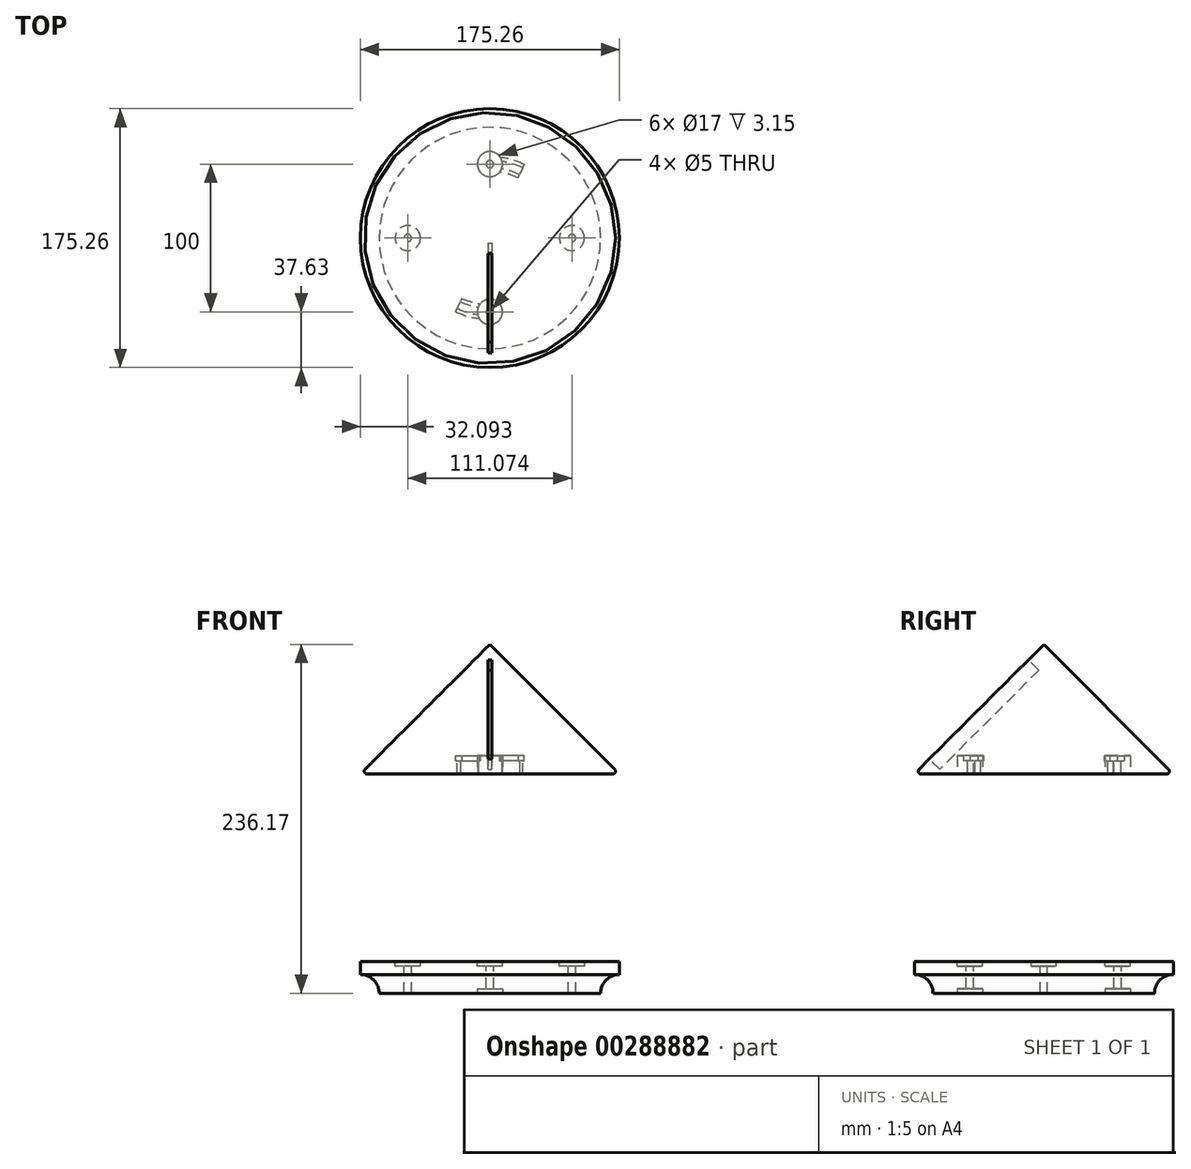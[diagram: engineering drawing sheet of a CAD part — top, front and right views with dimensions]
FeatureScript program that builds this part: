
annotation { "Feature Type Name" : "Feature", "Feature Type Description" : "" }
export const myFeature = defineFeature(function(context is Context, id is Id, definition is map)
    precondition{}
    {
        {
            var Q0;
            Q0=qCreatedBy(makeId("Front.planeOp"),FACE);
            var sketch = newSketch(context, id + "F0", { "sketchPlane" : qUnion([Q0])});
            skLineSegment(sketch, "E0", {"start": v(0, 0) * mm, "end": v(74.93, 0) * mm});
            skLineSegment(sketch, "E1", {"start": v(74.93, 0) * mm, "end": v(87.63, 0) * mm, "construction": true});
            skLineSegment(sketch, "E2", {"start": v(87.63, 0) * mm, "end": v(87.63, 12.7) * mm, "construction": true});
            skLineSegment(sketch, "E3", {"start": v(87.63, 12.7) * mm, "end": v(87.63, 21.35) * mm});
            skLineSegment(sketch, "E4", {"start": v(87.63, 21.35) * mm, "end": v(0, 21.35) * mm});
            skLineSegment(sketch, "E5", {"start": v(0, 21.35) * mm, "end": v(0, 0) * mm});
            skArc(sketch, "E6", {"start": v(87.63, 12.7) * mm, "mid": v(78.65, 8.98) * mm, "end": v(74.93, 0) * mm});
            skSolve(sketch);
        }
        {
            var Q0;
            Q0=makeQuery(id+"F0.imprint","IMPRINT",FACE,{"disambiguationData":[TD([[makeQuery(id+"F0.imprint","IMPRINT",EDGE,{"derivedFrom":sQuery(id+"F0.wireOp",EDGE,"E0")}),1.0]])]});
            var Q1;
            Q1=sQuery(id+"F0.wireOp",EDGE,"E5");
            revolve(context, id + "F1", {"entities" : qUnion([Q0]), "axis" : qUnion([Q1]), "revolveType" : RevolveType.FULL});
        }
        {
            var Q0;
            Q0=makeQuery(id+"F1.opRevolve","SWEPT_FACE",FACE,{"disambiguationData":[OSD([sQuery(id+"F0.wireOp",EDGE,"E4")])]});
            var sketch = newSketch(context, id + "F2", { "sketchPlane" : qUnion([Q0])});
            skPoint(sketch, "E7", {"position": v(55.54, 0) * mm});
            skPoint(sketch, "E8", {"position": v(-55.54, 0) * mm});
            skSolve(sketch);
        }
        {
            var Q0;
            Q0=sQuery(id+"F2.wireOp",VERTEX,"E8");
            var Q1;
            Q1=sQuery(id+"F2.wireOp",VERTEX,"E7");
            var Q2;
            Q2=makeQuery(id+"F1.opRevolve","SWEPT_BODY",BODY,{"disambiguationData":[OSD([sQuery(id+"F0.wireOp",EDGE,"E0"),sQuery(id+"F0.wireOp",EDGE,"E3"),sQuery(id+"F0.wireOp",EDGE,"E4"),sQuery(id+"F0.wireOp",EDGE,"E5"),sQuery(id+"F0.wireOp",EDGE,"E6")])]});
            hole(context, id + "F3", {"style" : HoleStyle.C_BORE, "endStyle" : HoleEndStyle.THROUGH, "holeDiameter" : 5 * mm, "cBoreDiameter" : 17 * mm, "cBoreDepth" : 3.15 * mm, "tappedDepth" : 12.7 * mm, "tapClearance" : 3, "locations" : qUnion([Q0, Q1]), "scope" : qUnion([Q2])});
        }
        {
            var Q0;
            Q0=makeQuery(id+"F1.opRevolve","SWEPT_FACE",FACE,{"disambiguationData":[OSD([sQuery(id+"F0.wireOp",EDGE,"E4")])]});
            var sketch = newSketch(context, id + "F4", { "sketchPlane" : qUnion([Q0])});
            skPoint(sketch, "E9", {"position": v(0, 50) * mm});
            skPoint(sketch, "E10", {"position": v(0, -50) * mm});
            skSolve(sketch);
        }
        {
            var Q0;
            Q0=sQuery(id+"F4.wireOp",VERTEX,"E9");
            var Q1;
            Q1=sQuery(id+"F4.wireOp",VERTEX,"E10");
            var Q2;
            Q2=makeQuery(id+"F1.opRevolve","SWEPT_BODY",BODY,{"disambiguationData":[OSD([sQuery(id+"F0.wireOp",EDGE,"E0"),sQuery(id+"F0.wireOp",EDGE,"E3"),sQuery(id+"F0.wireOp",EDGE,"E4"),sQuery(id+"F0.wireOp",EDGE,"E5"),sQuery(id+"F0.wireOp",EDGE,"E6")])]});
            hole(context, id + "F5", {"style" : HoleStyle.C_BORE, "endStyle" : HoleEndStyle.THROUGH, "holeDiameter" : 5 * mm, "cBoreDiameter" : 17 * mm, "cBoreDepth" : 3.15 * mm, "tappedDepth" : 12.7 * mm, "tapClearance" : 3, "locations" : qUnion([Q0, Q1]), "scope" : qUnion([Q2])});
        }
        {
            var Q0;
            Q0=makeQuery(id+"F1.opRevolve","SWEPT_FACE",FACE,{"disambiguationData":[OSD([sQuery(id+"F0.wireOp",EDGE,"E0")])]});
            var sketch = newSketch(context, id + "F6", { "sketchPlane" : qUnion([Q0])});
            skPoint(sketch, "E11", {"position": v(0, 50) * mm});
            skPoint(sketch, "E12", {"position": v(0, -50) * mm});
            skSolve(sketch);
        }
        {
            var Q0;
            Q0=sQuery(id+"F6.wireOp",VERTEX,"E11");
            var Q1;
            Q1=sQuery(id+"F6.wireOp",VERTEX,"E12");
            var Q2;
            Q2=makeQuery(id+"F1.opRevolve","SWEPT_BODY",BODY,{"disambiguationData":[OSD([sQuery(id+"F0.wireOp",EDGE,"E0"),sQuery(id+"F0.wireOp",EDGE,"E3"),sQuery(id+"F0.wireOp",EDGE,"E4"),sQuery(id+"F0.wireOp",EDGE,"E5"),sQuery(id+"F0.wireOp",EDGE,"E6")])]});
            hole(context, id + "F7", {"style" : HoleStyle.C_BORE, "endStyle" : HoleEndStyle.BLIND, "holeDiameter" : 4 * mm, "cBoreDiameter" : 17 * mm, "cBoreDepth" : 3.15 * mm, "holeDepth" : 3.15 * mm, "tappedDepth" : 12.7 * mm, "tapClearance" : 3, "locations" : qUnion([Q0, Q1]), "scope" : qUnion([Q2])});
        }
        {
            var Q0;
            Q0=makeQuery(id+"F1.opRevolve","SWEPT_FACE",FACE,{"disambiguationData":[OSD([sQuery(id+"F0.wireOp",EDGE,"E4")])]});
            cPlane(context, id + "F8", {"entities" : qUnion([Q0]), "cplaneType" : CPlaneType.OFFSET, "offset" : 127 * mm, "width" : 152.4 * mm, "height" : 152.4 * mm});
        }
        {
            var Q0;
            Q0=qCreatedBy(id+"F8.planeOp",FACE);
            var sketch = newSketch(context, id + "F9", { "sketchPlane" : qUnion([Q0])});
            skCircle(sketch, "E13.0", {"center": v(0, -50) * mm, "radius": 8.5 * mm, "construction": true});
            skCircle(sketch, "E13.1", {"center": v(0, 50) * mm, "radius": 8.5 * mm, "construction": true});
            skCircle(sketch, "E14.0", {"center": v(0, -50) * mm, "radius": 2.5 * mm, "construction": true});
            skCircle(sketch, "E14.1", {"center": v(0, 50) * mm, "radius": 2.5 * mm, "construction": true});
            skLineSegment(sketch, "E15", {"start": v(0, 126.36) * mm, "end": v(0, -138.85) * mm, "construction": true});
            skCircle(sketch, "E16.0", {"center": v(0, 0) * mm, "radius": 87.63 * mm, "construction": true});
            skCircle(sketch, "E17.0", {"center": v(0, 0) * mm, "radius": 74.93 * mm, "construction": true});
            skPoint(sketch, "E18", {"position": v(0, 87.63) * mm});
            skPoint(sketch, "E19", {"position": v(0, 74.93) * mm});
            skPoint(sketch, "E20", {"position": v(0, -74.93) * mm});
            skPoint(sketch, "E21", {"position": v(0, -87.63) * mm});
            skSolve(sketch);
        }
        {
            var Q0;
            Q0=qCreatedBy(makeId("Right.planeOp"),FACE);
            var sketch = newSketch(context, id + "F10", { "sketchPlane" : qUnion([Q0])});
            skLineSegment(sketch, "E22.1", {"start": v(-52.5, 148.35) * mm, "end": v(-47.5, 148.35) * mm});
            skLineSegment(sketch, "E23", {"start": v(0, 148.35) * mm, "end": v(-87.82, 148.35) * mm});
            skLineSegment(sketch, "E24", {"start": v(-87.82, 148.35) * mm, "end": v(0, 236.17) * mm});
            skLineSegment(sketch, "E25", {"start": v(0, 148.35) * mm, "end": v(0, 236.17) * mm});
            skLineSegment(sketch, "E26", {"start": v(-52.5, 148.35) * mm, "end": v(-52.5, 157.24) * mm});
            skLineSegment(sketch, "E27", {"start": v(-52.5, 157.24) * mm, "end": v(-55, 157.24) * mm});
            skLineSegment(sketch, "E28", {"start": v(-55, 157.24) * mm, "end": v(-55, 160.74) * mm});
            skLineSegment(sketch, "E29", {"start": v(-55, 160.74) * mm, "end": v(-50, 160.74) * mm});
            skPoint(sketch, "E29.endSnap0", {"position": v(-50, 148.35) * mm});
            skLineSegment(sketch, "E30", {"start": v(-50, 160.74) * mm, "end": v(-45, 160.74) * mm});
            skLineSegment(sketch, "E31", {"start": v(-45, 160.74) * mm, "end": v(-45, 157.24) * mm});
            skLineSegment(sketch, "E32", {"start": v(-45, 157.24) * mm, "end": v(-47.5, 157.24) * mm});
            skLineSegment(sketch, "E33", {"start": v(-47.5, 157.24) * mm, "end": v(-47.5, 148.35) * mm});
            skLineSegment(sketch, "E34.MirrorCS", {"start": v(52.5, 148.35) * mm, "end": v(47.5, 148.35) * mm, "construction": true});
            skLineSegment(sketch, "E35.MirrorCS", {"start": v(50, 160.74) * mm, "end": v(45, 160.74) * mm});
            skLineSegment(sketch, "E36.MirrorCS", {"start": v(45, 160.74) * mm, "end": v(45, 157.24) * mm});
            skLineSegment(sketch, "E37.MirrorCS", {"start": v(55, 157.24) * mm, "end": v(55, 160.74) * mm});
            skLineSegment(sketch, "E38.MirrorCS", {"start": v(45, 157.24) * mm, "end": v(47.5, 157.24) * mm});
            skLineSegment(sketch, "E39.MirrorCS", {"start": v(52.5, 157.24) * mm, "end": v(55, 157.24) * mm});
            skLineSegment(sketch, "E40.MirrorCS", {"start": v(47.5, 157.24) * mm, "end": v(47.5, 148.35) * mm});
            skLineSegment(sketch, "E41.MirrorCS", {"start": v(52.5, 148.35) * mm, "end": v(52.5, 157.24) * mm});
            skLineSegment(sketch, "E42.MirrorCS", {"start": v(55, 160.74) * mm, "end": v(50, 160.74) * mm});
            skPoint(sketch, "E43.MirrorP", {"position": v(50, 148.35) * mm});
            skLineSegment(sketch, "E44", {"start": v(52.5, 148.35) * mm, "end": v(47.5, 148.35) * mm});
            skSolve(sketch);
        }
        {
            var Q0;
            Q0=makeQuery(id+"F10.imprint","IMPRINT",FACE,{"disambiguationData":[TD([[makeQuery(id+"F10.imprint","IMPRINT",EDGE,{"derivedFrom":sQuery(id+"F10.wireOp",EDGE,"E27")}),-1.0]])]});
            var Q1;
            {var subQ3=sQuery(id+"F10.wireOp",EDGE,"E24");Q1=makeQuery(id+"F10.imprint","IMPRINT",FACE,{"disambiguationData":[TD([[makeQuery(id+"F10.imprint","IMPRINT",EDGE,{"derivedFrom":subQ3}),-1.0]])]});}
            var Q2;
            Q2=sQuery(id+"F10.wireOp",EDGE,"E25");
            revolve(context, id + "F11", {"entities" : qUnion([Q0, Q1]), "axis" : qUnion([Q2]), "revolveType" : RevolveType.FULL});
        }
        {
            var Q0;
            Q0=makeQuery(id+"F10.imprint","IMPRINT",FACE,{"disambiguationData":[TD([[makeQuery(id+"F10.imprint","IMPRINT",EDGE,{"derivedFrom":sQuery(id+"F10.wireOp",EDGE,"E27")}),-1.0]])]});
            var Q1;
            Q1=makeQuery(id+"F10.imprint","IMPRINT",FACE,{"disambiguationData":[TD([[makeQuery(id+"F10.imprint","IMPRINT",EDGE,{"derivedFrom":sQuery(id+"F10.wireOp",EDGE,"E35.MirrorCS")}),1.0]])]});
            var Q2;
            Q2=sQuery(id+"F10.wireOp",EDGE,"E25");
            revolve(context, id + "F12", {"entities" : qUnion([Q0, Q1]), "axis" : qUnion([Q2]), "revolveType" : RevolveType.ONE_DIRECTION, "oppositeDirection" : true, "angle" : 25 * degree});
        }
        {
            var Q0;
            Q0=makeQuery(id+"F12.opRevolve","SWEPT_BODY",BODY,{"disambiguationData":[OSD([sQuery(id+"F10.wireOp",EDGE,"E23"),sQuery(id+"F10.wireOp",EDGE,"E27"),sQuery(id+"F10.wireOp",EDGE,"E28"),sQuery(id+"F10.wireOp",EDGE,"E29"),sQuery(id+"F10.wireOp",EDGE,"E30"),sQuery(id+"F10.wireOp",EDGE,"E31"),sQuery(id+"F10.wireOp",EDGE,"E32"),sQuery(id+"F10.wireOp",EDGE,"E33"),sQuery(id+"F10.wireOp",EDGE,"E26")])]});
            var Q1;
            Q1=makeQuery(id+"F12.opRevolve","SWEPT_BODY",BODY,{"disambiguationData":[OSD([sQuery(id+"F10.wireOp",EDGE,"E35.MirrorCS"),sQuery(id+"F10.wireOp",EDGE,"E36.MirrorCS"),sQuery(id+"F10.wireOp",EDGE,"E37.MirrorCS"),sQuery(id+"F10.wireOp",EDGE,"E38.MirrorCS"),sQuery(id+"F10.wireOp",EDGE,"E39.MirrorCS"),sQuery(id+"F10.wireOp",EDGE,"E40.MirrorCS"),sQuery(id+"F10.wireOp",EDGE,"E41.MirrorCS"),sQuery(id+"F10.wireOp",EDGE,"E42.MirrorCS"),sQuery(id+"F10.wireOp",EDGE,"E44")])]});
            var Q2;
            Q2=makeQuery(id+"F11.opRevolve","SWEPT_BODY",BODY,{"disambiguationData":[OSD([sQuery(id+"F10.wireOp",EDGE,"E23"),sQuery(id+"F10.wireOp",EDGE,"E24"),sQuery(id+"F10.wireOp",EDGE,"E25")])]});
            booleanBodies(context, id + "F13", {"operationType" : BooleanOperationType.SUBTRACTION, "tools" : qUnion([Q0, Q1]), "targets" : qUnion([Q2])});
        }
        {
            var Q0;
            Q0=makeQuery(id+"F11.opRevolve","SWEPT_FACE",FACE,{"disambiguationData":[OSD([sQuery(id+"F10.wireOp",EDGE,"E23")])]});
            var sketch = newSketch(context, id + "F14", { "sketchPlane" : qUnion([Q0])});
            skCircle(sketch, "E45.0", {"center": v(0, -50) * mm, "radius": 8.5 * mm});
            skCircle(sketch, "E45.1", {"center": v(0, 50) * mm, "radius": 8.5 * mm});
            skSolve(sketch);
        }
        {
            var Q0;
            Q0 = qSketchRegion(id + "F14", true);
            var Q1;
            Q1=makeQuery(id+"F13.opBoolean","COPY",FACE,{"derivedFrom":makeQuery(id+"F12.opRevolve","SWEPT_FACE",FACE,{"disambiguationData":[OSD([sQuery(id+"F10.wireOp",EDGE,"E29"),sQuery(id+"F10.wireOp",EDGE,"E30")])]})});
            var Q2;
            Q2=makeQuery(id+"F13.opBoolean","COPY",FACE,{"derivedFrom":makeQuery(id+"F12.opRevolve","SWEPT_FACE",FACE,{"disambiguationData":[OSD([sQuery(id+"F10.wireOp",EDGE,"E29"),sQuery(id+"F10.wireOp",EDGE,"E30")])]})});
            extrude(context, id + "F15", {"entities" : qUnion([Q0]), "operationType" : NewBodyOperationType.REMOVE, "endBound" : BoundingType.UP_TO_SURFACE, "oppositeDirection" : true, "endBoundEntityFace" : qUnion([Q1]), "depth" : 25.4 * mm});
        }
        {
            var Q0;
            Q0=makeQuery(id+"F11.opRevolve","SWEPT_EDGE",EDGE,{"disambiguationData":[OSD([sQuery(id+"F10.wireOp",EDGE,"E23"),sQuery(id+"F10.wireOp",EDGE,"E24")])]});
            fillet(context, id + "F16", {"entities" : qUnion([Q0]), "radius" : 2 * mm, "tangentPropagation" : true, "allowEdgeOverflow" : false});
        }
        {
            var Q0;
            Q0=sQuery(id+"F10.wireOp",EDGE,"E24");
            cPlane(context, id + "F17", {"entities" : qUnion([Q0]), "cplaneType" : CPlaneType.LINE_ANGLE, "offset" : 25.4 * mm, "angle" : 0 * degree, "width" : 152.4 * mm, "height" : 152.4 * mm});
        }
        {
            var Q0;
            Q0=qCreatedBy(id+"F17.planeOp",FACE);
            var sketch = newSketch(context, id + "F18", { "sketchPlane" : qUnion([Q0])});
            skLineSegment(sketch, "E46.0", {"start": v(0, 42.8) * mm, "end": v(0, 167) * mm, "construction": true});
            skLineSegment(sketch, "E47.bottom", {"start": v(-1.25, 152.3) * mm, "end": v(1.25, 152.3) * mm});
            skLineSegment(sketch, "E47.top", {"start": v(-1.25, 57.3) * mm, "end": v(1.25, 57.3) * mm});
            skLineSegment(sketch, "E47.left", {"start": v(-1.25, 152.3) * mm, "end": v(-1.25, 57.3) * mm});
            skLineSegment(sketch, "E47.right", {"start": v(1.25, 152.3) * mm, "end": v(1.25, 57.3) * mm});
            skSolve(sketch);
        }
        {
            var Q0;
            Q0=makeQuery(id+"F18.imprint","IMPRINT",FACE,{"disambiguationData":[TD([[makeQuery(id+"F18.imprint","IMPRINT",EDGE,{"derivedFrom":sQuery(id+"F18.wireOp",EDGE,"E47.bottom")}),-1.0]])]});
            extrude(context, id + "F19", {"entities" : qUnion([Q0]), "operationType" : NewBodyOperationType.REMOVE, "oppositeDirection" : true, "depth" : 10 * mm});
        }
    });
